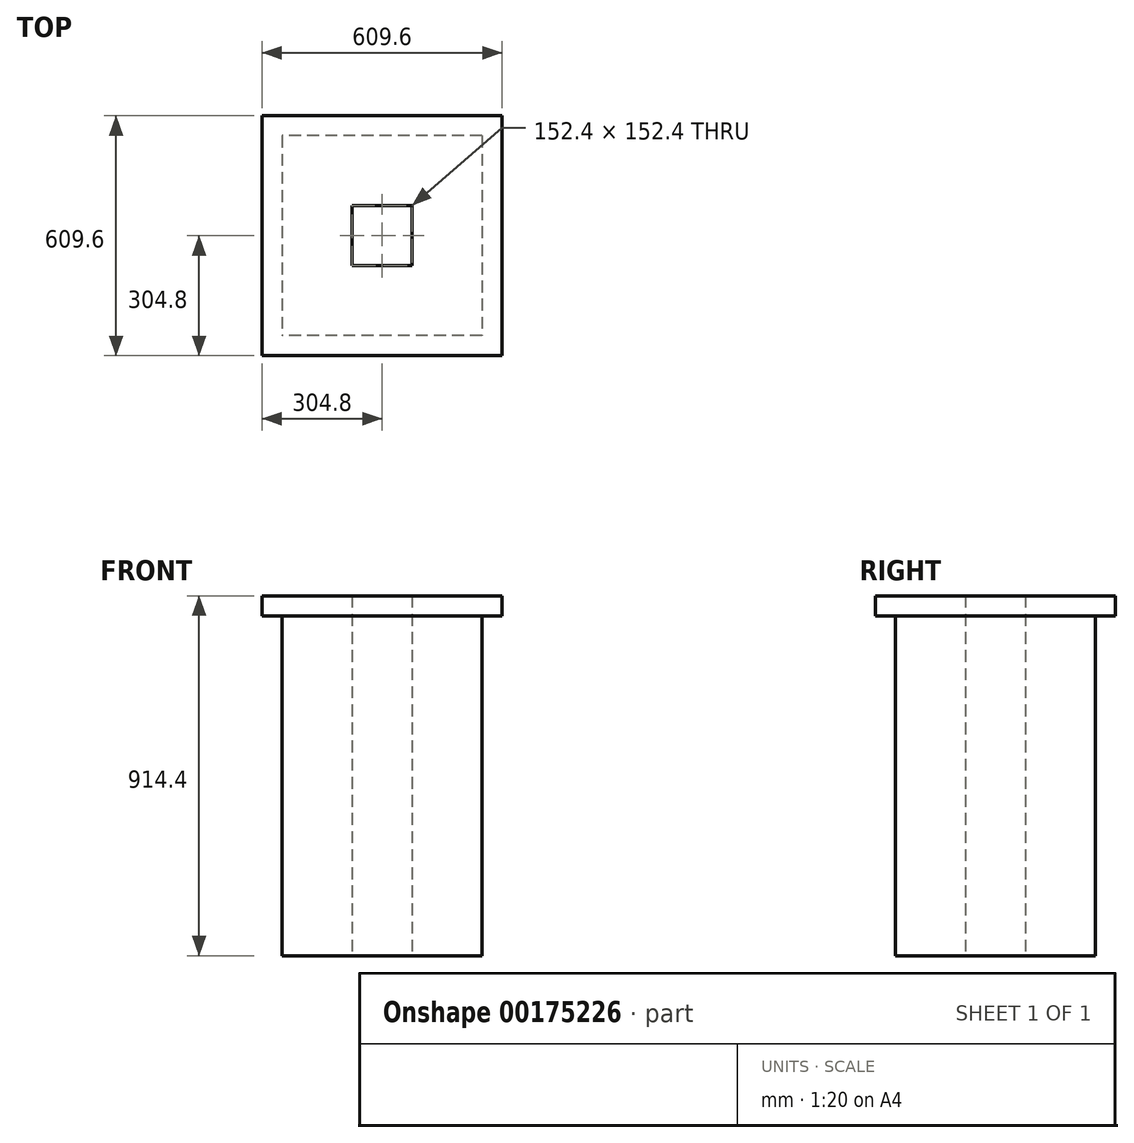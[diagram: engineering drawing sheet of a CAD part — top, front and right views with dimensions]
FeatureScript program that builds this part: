
annotation { "Feature Type Name" : "Feature", "Feature Type Description" : "" }
export const myFeature = defineFeature(function(context is Context, id is Id, definition is map)
    precondition{}
    {
        {
            var Q0;
            Q0=qCreatedBy(makeId("Top.planeOp"),FACE);
            var sketch = newSketch(context, id + "F0", { "sketchPlane" : qUnion([Q0])});
            skLineSegment(sketch, "E0.bottom", {"start": v(76.2, 76.2) * mm, "end": v(-76.2, 76.2) * mm});
            skLineSegment(sketch, "E0.top", {"start": v(76.2, -76.2) * mm, "end": v(-76.2, -76.2) * mm});
            skLineSegment(sketch, "E0.left", {"start": v(76.2, 76.2) * mm, "end": v(76.2, -76.2) * mm});
            skLineSegment(sketch, "E0.right", {"start": v(-76.2, 76.2) * mm, "end": v(-76.2, -76.2) * mm});
            skPoint(sketch, "E0.middle", {"position": v(0, 0) * mm});
            skLineSegment(sketch, "E1.bottom", {"start": v(254, 254) * mm, "end": v(-254, 254) * mm});
            skLineSegment(sketch, "E1.top", {"start": v(254, -254) * mm, "end": v(-254, -254) * mm});
            skLineSegment(sketch, "E1.left", {"start": v(254, 254) * mm, "end": v(254, -254) * mm});
            skLineSegment(sketch, "E1.right", {"start": v(-254, 254) * mm, "end": v(-254, -254) * mm});
            skSolve(sketch);
        }
        {
            var Q0;
            Q0=makeQuery(id+"F0.imprint","IMPRINT",FACE,{"disambiguationData":[TD([[makeQuery(id+"F0.imprint","IMPRINT",EDGE,{"derivedFrom":sQuery(id+"F0.wireOp",EDGE,"E0.bottom")}),-1.0]])]});
            extrude(context, id + "F1", {"entities" : qUnion([Q0]), "depth" : 863.6 * mm});
        }
        {
            var Q0;
            Q0=makeQuery(id+"F1.opExtrude","CAP_FACE",FACE,{"disambiguationData":[OSD([sQuery(id+"F0.wireOp",EDGE,"E0.bottom"),sQuery(id+"F0.wireOp",EDGE,"E0.top"),sQuery(id+"F0.wireOp",EDGE,"E0.left"),sQuery(id+"F0.wireOp",EDGE,"E0.right"),sQuery(id+"F0.wireOp",EDGE,"E1.bottom"),sQuery(id+"F0.wireOp",EDGE,"E1.top"),sQuery(id+"F0.wireOp",EDGE,"E1.left"),sQuery(id+"F0.wireOp",EDGE,"E1.right")])],"isStart":false});
            var sketch = newSketch(context, id + "F2", { "sketchPlane" : qUnion([Q0])});
            skLineSegment(sketch, "E2.bottom", {"start": v(304.8, 304.8) * mm, "end": v(-304.8, 304.8) * mm});
            skLineSegment(sketch, "E2.top", {"start": v(304.8, -304.8) * mm, "end": v(-304.8, -304.8) * mm});
            skLineSegment(sketch, "E2.left", {"start": v(304.8, 304.8) * mm, "end": v(304.8, -304.8) * mm});
            skLineSegment(sketch, "E2.right", {"start": v(-304.8, 304.8) * mm, "end": v(-304.8, -304.8) * mm});
            skPoint(sketch, "E2.middle", {"position": v(0, 0) * mm});
            skSolve(sketch);
        }
        {
            var Q0;
            Q0 = qSketchRegion(id + "F2", true);
            extrude(context, id + "F3", {"entities" : qUnion([Q0]), "operationType" : NewBodyOperationType.ADD, "depth" : 50.8 * mm});
        }
        {
            var Q0;
            Q0=makeQuery(id+"F3.opExtrude","CAP_FACE",FACE,{"disambiguationData":[OSD([sQuery(id+"F2.wireOp",EDGE,"E2.bottom"),sQuery(id+"F2.wireOp",EDGE,"E2.top"),sQuery(id+"F2.wireOp",EDGE,"E2.left"),sQuery(id+"F2.wireOp",EDGE,"E2.right")])],"isStart":false});
            var sketch = newSketch(context, id + "F4", { "sketchPlane" : qUnion([Q0])});
            skLineSegment(sketch, "E3.bottom", {"start": v(76.2, 76.2) * mm, "end": v(-76.2, 76.2) * mm});
            skLineSegment(sketch, "E3.top", {"start": v(76.2, -76.2) * mm, "end": v(-76.2, -76.2) * mm});
            skLineSegment(sketch, "E3.left", {"start": v(76.2, 76.2) * mm, "end": v(76.2, -76.2) * mm});
            skLineSegment(sketch, "E3.right", {"start": v(-76.2, 76.2) * mm, "end": v(-76.2, -76.2) * mm});
            skPoint(sketch, "E3.middle", {"position": v(0, 0) * mm});
            skSolve(sketch);
        }
        {
            var Q0;
            Q0=makeQuery(id+"F4.imprint","IMPRINT",FACE,{"disambiguationData":[TD([[makeQuery(id+"F4.imprint","IMPRINT",EDGE,{"derivedFrom":sQuery(id+"F4.wireOp",EDGE,"E3.bottom")}),1.0]])]});
            extrude(context, id + "F5", {"entities" : qUnion([Q0]), "operationType" : NewBodyOperationType.REMOVE, "oppositeDirection" : true, "depth" : 254 * mm});
        }
    });
